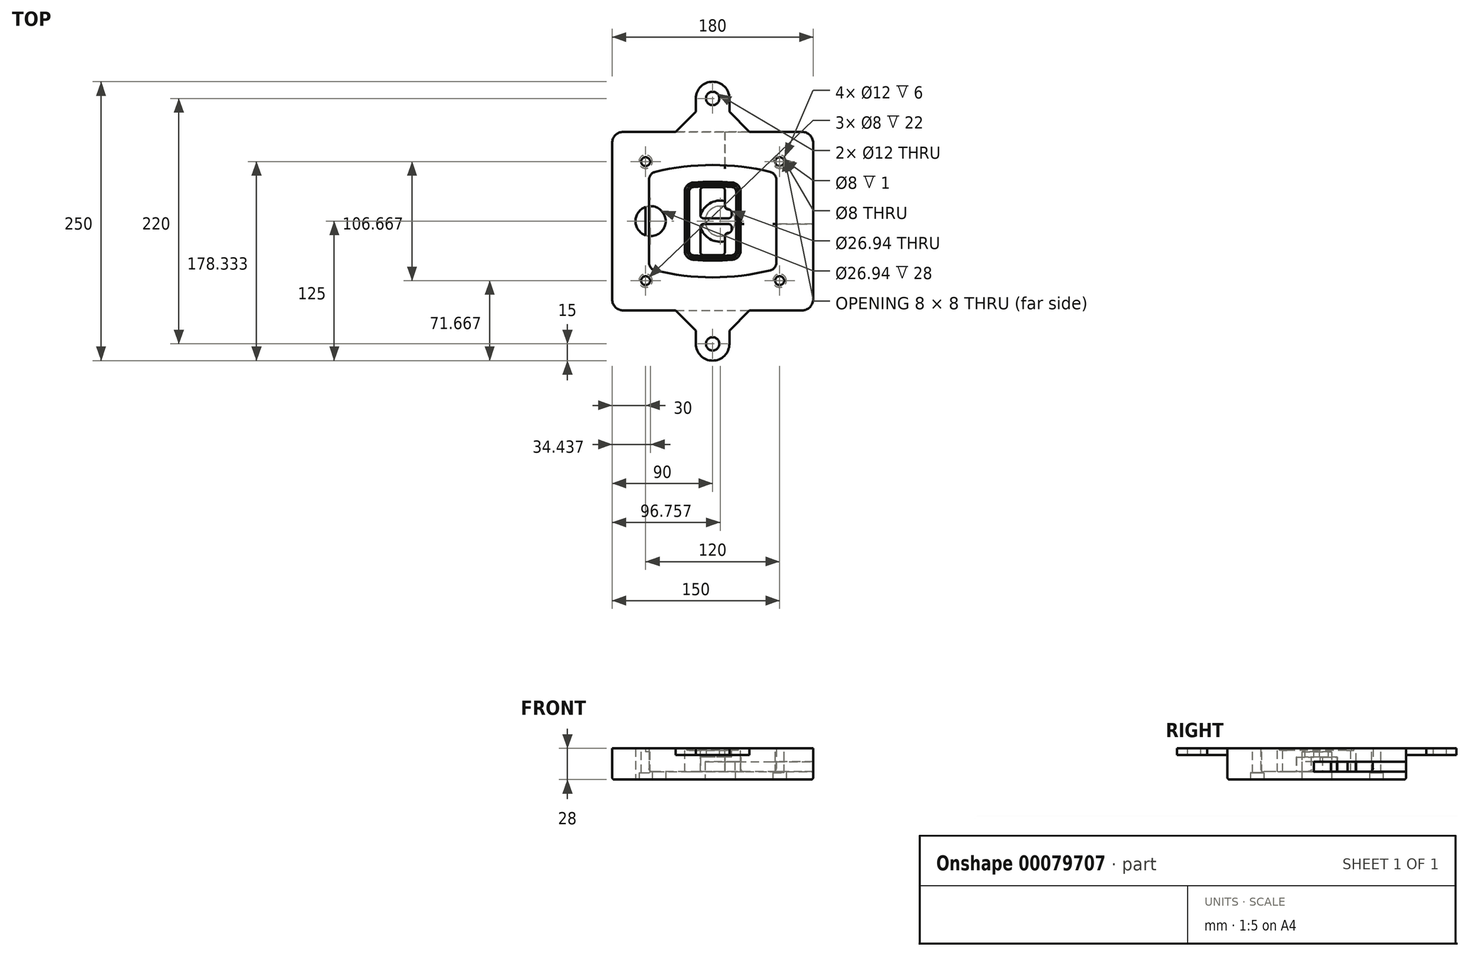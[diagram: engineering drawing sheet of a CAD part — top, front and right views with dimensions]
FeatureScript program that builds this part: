
annotation { "Feature Type Name" : "Feature", "Feature Type Description" : "" }
export const myFeature = defineFeature(function(context is Context, id is Id, definition is map)
    precondition{}
    {
        {
            var Q0;
            Q0=qCreatedBy(makeId("Top.planeOp"),FACE);
            var sketch = newSketch(context, id + "F0", { "sketchPlane" : qUnion([Q0])});
            skPoint(sketch, "E0.rect.middle", {"position": v(0, 0) * mm});
            skLineSegment(sketch, "E1.bottom", {"start": v(-80, -80) * mm, "end": v(80, -80) * mm});
            skLineSegment(sketch, "E1.top", {"start": v(-80, 80) * mm, "end": v(80, 80) * mm});
            skLineSegment(sketch, "E1.left", {"start": v(-90, -70) * mm, "end": v(-90, 70) * mm});
            skLineSegment(sketch, "E1.right", {"start": v(90, -70) * mm, "end": v(90, 70) * mm});
            skLineSegment(sketch, "E2", {"start": v(-90, 80) * mm, "end": v(90, -80) * mm, "construction": true});
            skLineSegment(sketch, "E3", {"start": v(90, 80) * mm, "end": v(-90, -80) * mm, "construction": true});
            skCircle(sketch, "E4", {"center": v(-60, 53.33) * mm, "radius": 4 * mm});
            skCircle(sketch, "E5", {"center": v(60, 53.33) * mm, "radius": 4 * mm});
            skCircle(sketch, "E6", {"center": v(60, -53.33) * mm, "radius": 4 * mm});
            skCircle(sketch, "E7", {"center": v(-60, -53.33) * mm, "radius": 4 * mm});
            skLineSegment(sketch, "E8", {"start": v(-60, 53.33) * mm, "end": v(60, 53.33) * mm, "construction": true});
            skLineSegment(sketch, "E9", {"start": v(60, 53.33) * mm, "end": v(60, -53.33) * mm, "construction": true});
            skLineSegment(sketch, "E10", {"start": v(60, -53.33) * mm, "end": v(-60, -53.33) * mm, "construction": true});
            skLineSegment(sketch, "E11", {"start": v(-60, -53.33) * mm, "end": v(-60, 53.33) * mm, "construction": true});
            skLineSegment(sketch, "E12", {"start": v(-60, 37.3) * mm, "end": v(-60, -37.3) * mm});
            skLineSegment(sketch, "E13", {"start": v(60, 37.3) * mm, "end": v(60, -37.3) * mm});
            skArc(sketch, "E14", {"start": v(52.38, 47.01) * mm, "mid": v(0, 53.33) * mm, "end": v(-52.38, 47.01) * mm});
            skArc(sketch, "E15", {"start": v(-52.38, -47.01) * mm, "mid": v(0, -53.33) * mm, "end": v(52.38, -47.01) * mm});
            skLineSegment(sketch, "E16", {"start": v(-60, 0) * mm, "end": v(60, 0) * mm, "construction": true});
            skPoint(sketch, "E17.visualSharp", {"position": v(-60, -45) * mm});
            skArc(sketch, "E17.filletArc", {"start": v(-60, -37.3) * mm, "mid": v(-57.87, -43.47) * mm, "end": v(-52.38, -47.01) * mm});
            skPoint(sketch, "E18.visualSharp", {"position": v(-60, 45) * mm});
            skArc(sketch, "E18.filletArc", {"start": v(-52.38, 47.01) * mm, "mid": v(-57.87, 43.47) * mm, "end": v(-60, 37.3) * mm});
            skPoint(sketch, "E19.visualSharp", {"position": v(60, 45) * mm});
            skArc(sketch, "E19.filletArc", {"start": v(60, 37.3) * mm, "mid": v(57.87, 43.47) * mm, "end": v(52.38, 47.01) * mm});
            skPoint(sketch, "E20.visualSharp", {"position": v(60, -45) * mm});
            skArc(sketch, "E20.filletArc", {"start": v(52.38, -47.01) * mm, "mid": v(57.87, -43.47) * mm, "end": v(60, -37.3) * mm});
            skPoint(sketch, "E21.visualSharp", {"position": v(-90, 80) * mm});
            skArc(sketch, "E21.filletArc", {"start": v(-80, 80) * mm, "mid": v(-87.07, 77.07) * mm, "end": v(-90, 70) * mm});
            skPoint(sketch, "E22.visualSharp", {"position": v(90, 80) * mm});
            skArc(sketch, "E22.filletArc", {"start": v(90, 70) * mm, "mid": v(87.07, 77.07) * mm, "end": v(80, 80) * mm});
            skPoint(sketch, "E23.visualSharp", {"position": v(90, -80) * mm});
            skArc(sketch, "E23.filletArc", {"start": v(80, -80) * mm, "mid": v(87.07, -77.07) * mm, "end": v(90, -70) * mm});
            skPoint(sketch, "E24.visualSharp", {"position": v(-90, -80) * mm});
            skArc(sketch, "E24.filletArc", {"start": v(-90, -70) * mm, "mid": v(-87.07, -77.07) * mm, "end": v(-80, -80) * mm});
            skArc(sketch, "E25.0", {"start": v(57, 37.3) * mm, "mid": v(55.5, 41.62) * mm, "end": v(51.67, 44.1) * mm});
            skLineSegment(sketch, "E25.1", {"start": v(57, 37.3) * mm, "end": v(57, -37.3) * mm});
            skArc(sketch, "E25.2", {"start": v(51.67, -44.1) * mm, "mid": v(55.5, -41.62) * mm, "end": v(57, -37.3) * mm});
            skArc(sketch, "E25.3", {"start": v(-51.67, -44.1) * mm, "mid": v(0, -50.33) * mm, "end": v(51.67, -44.1) * mm});
            skArc(sketch, "E25.4", {"start": v(-57, -37.3) * mm, "mid": v(-55.5, -41.62) * mm, "end": v(-51.67, -44.1) * mm});
            skArc(sketch, "E25.5", {"start": v(51.67, 44.1) * mm, "mid": v(0, 50.33) * mm, "end": v(-51.67, 44.1) * mm});
            skLineSegment(sketch, "E25.6", {"start": v(-57, 37.3) * mm, "end": v(-57, -37.3) * mm});
            skArc(sketch, "E25.7", {"start": v(-51.67, 44.1) * mm, "mid": v(-55.5, 41.62) * mm, "end": v(-57, 37.3) * mm});
            skArc(sketch, "E26.0", {"start": v(-53.33, 50.9) * mm, "mid": v(-61.01, 45.94) * mm, "end": v(-64, 37.3) * mm});
            skArc(sketch, "E26.1", {"start": v(53.33, 50.9) * mm, "mid": v(0, 57.33) * mm, "end": v(-53.33, 50.9) * mm});
            skArc(sketch, "E26.2", {"start": v(64, 37.3) * mm, "mid": v(61.01, 45.94) * mm, "end": v(53.33, 50.9) * mm});
            skLineSegment(sketch, "E26.3", {"start": v(64, 37.3) * mm, "end": v(64, -37.3) * mm});
            skArc(sketch, "E26.4", {"start": v(53.33, -50.9) * mm, "mid": v(61.01, -45.94) * mm, "end": v(64, -37.3) * mm});
            skLineSegment(sketch, "E26.5", {"start": v(-64, 37.3) * mm, "end": v(-64, -37.3) * mm});
            skArc(sketch, "E26.6", {"start": v(-53.33, -50.9) * mm, "mid": v(0, -57.33) * mm, "end": v(53.33, -50.9) * mm});
            skArc(sketch, "E26.7", {"start": v(-64, -37.3) * mm, "mid": v(-61.01, -45.94) * mm, "end": v(-53.33, -50.9) * mm});
            skSolve(sketch);
        }
        {
            var Q0;
            Q0=makeQuery(id+"F0.imprint","IMPRINT",FACE,{"disambiguationData":[TD([[makeQuery(id+"F0.imprint","IMPRINT",EDGE,{"derivedFrom":sQuery(id+"F0.wireOp",EDGE,"E1.bottom")}),1.0]])]});
            var Q1;
            Q1=makeQuery(id+"F0.imprint","IMPRINT",FACE,{"disambiguationData":[TD([[makeQuery(id+"F0.imprint","IMPRINT",EDGE,{"derivedFrom":sQuery(id+"F0.wireOp",EDGE,"E12")}),1.0]])]});
            var Q2;
            Q2=makeQuery(id+"F0.imprint","IMPRINT",FACE,{"disambiguationData":[TD([[makeQuery(id+"F0.imprint","IMPRINT",EDGE,{"derivedFrom":sQuery(id+"F0.wireOp",EDGE,"E25.0")}),1.0]])]});
            var Q3;
            Q3=makeQuery(id+"F0.imprint","IMPRINT",FACE,{"disambiguationData":[TD([[makeQuery(id+"F0.imprint","IMPRINT",EDGE,{"derivedFrom":sQuery(id+"F0.wireOp",EDGE,"E12")}),-1.0]])]});
            extrude(context, id + "F1", {"entities" : qUnion([Q0, Q1, Q2, Q3]), "oppositeDirection" : true, "depth" : 25 * mm});
        }
        {
            var Q0;
            Q0=makeQuery(id+"F0.imprint","IMPRINT",FACE,{"disambiguationData":[TD([[makeQuery(id+"F0.imprint","IMPRINT",EDGE,{"derivedFrom":sQuery(id+"F0.wireOp",EDGE,"E12")}),1.0]])]});
            extrude(context, id + "F2", {"entities" : qUnion([Q0]), "operationType" : NewBodyOperationType.ADD, "depth" : 3 * mm});
        }
        {
            var Q0;
            Q0=makeQuery(id+"F0.imprint","IMPRINT",FACE,{"disambiguationData":[TD([[makeQuery(id+"F0.imprint","IMPRINT",EDGE,{"derivedFrom":sQuery(id+"F0.wireOp",EDGE,"E25.0")}),1.0]])]});
            extrude(context, id + "F3", {"entities" : qUnion([Q0]), "operationType" : NewBodyOperationType.REMOVE, "oppositeDirection" : true, "depth" : 18 * mm});
        }
        {
            var Q0;
            Q0=makeQuery(id+"F2.opExtrude","CAP_FACE",FACE,{"disambiguationData":[OSD([sQuery(id+"F0.wireOp",EDGE,"E12"),sQuery(id+"F0.wireOp",EDGE,"E13"),sQuery(id+"F0.wireOp",EDGE,"E14"),sQuery(id+"F0.wireOp",EDGE,"E15"),sQuery(id+"F0.wireOp",EDGE,"E17.filletArc"),sQuery(id+"F0.wireOp",EDGE,"E18.filletArc"),sQuery(id+"F0.wireOp",EDGE,"E19.filletArc"),sQuery(id+"F0.wireOp",EDGE,"E20.filletArc"),sQuery(id+"F0.wireOp",EDGE,"E25.0"),sQuery(id+"F0.wireOp",EDGE,"E25.1"),sQuery(id+"F0.wireOp",EDGE,"E25.2"),sQuery(id+"F0.wireOp",EDGE,"E25.3"),sQuery(id+"F0.wireOp",EDGE,"E25.4"),sQuery(id+"F0.wireOp",EDGE,"E25.5"),sQuery(id+"F0.wireOp",EDGE,"E25.6"),sQuery(id+"F0.wireOp",EDGE,"E25.7")])],"isStart":false});
            var sketch = newSketch(context, id + "F4", { "sketchPlane" : qUnion([Q0])});
            skArc(sketch, "E27.0", {"start": v(-17.7, -34.56) * mm, "mid": v(0, -35.33) * mm, "end": v(17.7, -34.56) * mm});
            skArc(sketch, "E28.0", {"start": v(17.7, 34.56) * mm, "mid": v(0, 35.33) * mm, "end": v(-17.7, 34.56) * mm});
            skLineSegment(sketch, "E29", {"start": v(-25, 26.59) * mm, "end": v(-25, -26.59) * mm});
            skLineSegment(sketch, "E30", {"start": v(25, 26.59) * mm, "end": v(25, -26.59) * mm});
            skLineSegment(sketch, "E31", {"start": v(-25, 33.78) * mm, "end": v(25, 33.78) * mm, "construction": true});
            skLineSegment(sketch, "E32", {"start": v(-25, -33.78) * mm, "end": v(25, -33.78) * mm, "construction": true});
            skPoint(sketch, "E33.visualSharp", {"position": v(-25, 33.78) * mm});
            skArc(sketch, "E33.filletArc", {"start": v(-17.7, 34.56) * mm, "mid": v(-22.9, 32) * mm, "end": v(-25, 26.59) * mm});
            skPoint(sketch, "E34.visualSharp", {"position": v(25, 33.78) * mm});
            skArc(sketch, "E34.filletArc", {"start": v(25, 26.59) * mm, "mid": v(22.9, 32) * mm, "end": v(17.7, 34.56) * mm});
            skPoint(sketch, "E35.visualSharp", {"position": v(25, -33.78) * mm});
            skArc(sketch, "E35.filletArc", {"start": v(17.7, -34.56) * mm, "mid": v(22.9, -32) * mm, "end": v(25, -26.59) * mm});
            skPoint(sketch, "E36.visualSharp", {"position": v(-25, -33.78) * mm});
            skArc(sketch, "E36.filletArc", {"start": v(-25, -26.59) * mm, "mid": v(-22.9, -32) * mm, "end": v(-17.7, -34.56) * mm});
            skArc(sketch, "E37.0", {"start": v(51.67, 44.1) * mm, "mid": v(0, 50.33) * mm, "end": v(-51.67, 44.1) * mm});
            skArc(sketch, "E37.1", {"start": v(-51.67, 44.1) * mm, "mid": v(-55.5, 41.62) * mm, "end": v(-57, 37.3) * mm});
            skLineSegment(sketch, "E37.2", {"start": v(-57, 37.3) * mm, "end": v(-57, -37.3) * mm});
            skArc(sketch, "E37.3", {"start": v(-57, -37.3) * mm, "mid": v(-55.5, -41.62) * mm, "end": v(-51.67, -44.1) * mm});
            skArc(sketch, "E37.4", {"start": v(-51.67, -44.1) * mm, "mid": v(0, -50.33) * mm, "end": v(51.67, -44.1) * mm});
            skArc(sketch, "E37.5", {"start": v(51.67, -44.1) * mm, "mid": v(55.5, -41.62) * mm, "end": v(57, -37.3) * mm});
            skLineSegment(sketch, "E37.6", {"start": v(57, 37.3) * mm, "end": v(57, -37.3) * mm});
            skArc(sketch, "E37.7", {"start": v(57, 37.3) * mm, "mid": v(55.5, 41.62) * mm, "end": v(51.67, 44.1) * mm});
            skLineSegment(sketch, "E38.0", {"start": v(23, 26.59) * mm, "end": v(23, -26.59) * mm});
            skArc(sketch, "E38.1", {"start": v(17.53, -32.56) * mm, "mid": v(21.42, -30.64) * mm, "end": v(23, -26.59) * mm});
            skArc(sketch, "E38.2", {"start": v(-17.53, -32.56) * mm, "mid": v(0, -33.33) * mm, "end": v(17.53, -32.56) * mm});
            skArc(sketch, "E38.3", {"start": v(-23, -26.59) * mm, "mid": v(-21.42, -30.64) * mm, "end": v(-17.53, -32.56) * mm});
            skLineSegment(sketch, "E38.4", {"start": v(-23, 26.59) * mm, "end": v(-23, -26.59) * mm});
            skArc(sketch, "E38.5", {"start": v(23, 26.59) * mm, "mid": v(21.42, 30.64) * mm, "end": v(17.53, 32.56) * mm});
            skArc(sketch, "E38.6", {"start": v(-17.53, 32.56) * mm, "mid": v(-21.42, 30.64) * mm, "end": v(-23, 26.59) * mm});
            skArc(sketch, "E38.7", {"start": v(17.53, 32.56) * mm, "mid": v(0, 33.33) * mm, "end": v(-17.53, 32.56) * mm});
            skArc(sketch, "E39.0", {"start": v(21, 26.59) * mm, "mid": v(19.95, 29.29) * mm, "end": v(17.35, 30.57) * mm});
            skLineSegment(sketch, "E39.1", {"start": v(21, 26.59) * mm, "end": v(21, -26.59) * mm});
            skArc(sketch, "E39.2", {"start": v(17.35, -30.57) * mm, "mid": v(19.95, -29.29) * mm, "end": v(21, -26.59) * mm});
            skArc(sketch, "E39.3", {"start": v(-17.35, -30.57) * mm, "mid": v(0, -31.33) * mm, "end": v(17.35, -30.57) * mm});
            skArc(sketch, "E39.4", {"start": v(-21, -26.59) * mm, "mid": v(-19.95, -29.29) * mm, "end": v(-17.35, -30.57) * mm});
            skArc(sketch, "E39.5", {"start": v(17.35, 30.57) * mm, "mid": v(0, 31.33) * mm, "end": v(-17.35, 30.57) * mm});
            skLineSegment(sketch, "E39.6", {"start": v(-21, 26.59) * mm, "end": v(-21, -26.59) * mm});
            skArc(sketch, "E39.7", {"start": v(-17.35, 30.57) * mm, "mid": v(-19.95, 29.29) * mm, "end": v(-21, 26.59) * mm});
            skLineSegment(sketch, "E40", {"start": v(-25, 0) * mm, "end": v(25, 0) * mm, "construction": true});
            skLineSegment(sketch, "E41", {"start": v(-11, 5.5) * mm, "end": v(-11, 27.5) * mm});
            skLineSegment(sketch, "E42", {"start": v(-8, 30.5) * mm, "end": v(8, 30.5) * mm});
            skLineSegment(sketch, "E43", {"start": v(11, 27.5) * mm, "end": v(11, 13.5) * mm});
            skLineSegment(sketch, "E44", {"start": v(14, 10.5) * mm, "end": v(14, 10.5) * mm});
            skLineSegment(sketch, "E45", {"start": v(17, 7.5) * mm, "end": v(17, 5.5) * mm});
            skLineSegment(sketch, "E46", {"start": v(14, 2.5) * mm, "end": v(-8, 2.5) * mm});
            skPoint(sketch, "E47.visualSharp", {"position": v(-11, 30.5) * mm});
            skArc(sketch, "E47.filletArc", {"start": v(-8, 30.5) * mm, "mid": v(-10.12, 29.62) * mm, "end": v(-11, 27.5) * mm});
            skPoint(sketch, "E48.visualSharp", {"position": v(11, 30.5) * mm});
            skArc(sketch, "E48.filletArc", {"start": v(11, 27.5) * mm, "mid": v(10.12, 29.62) * mm, "end": v(8, 30.5) * mm});
            skPoint(sketch, "E49.visualSharp", {"position": v(11, 10.5) * mm});
            skArc(sketch, "E49.filletArc", {"start": v(11, 13.5) * mm, "mid": v(11.88, 11.38) * mm, "end": v(14, 10.5) * mm});
            skPoint(sketch, "E50.visualSharp", {"position": v(17, 10.5) * mm});
            skArc(sketch, "E50.filletArc", {"start": v(17, 7.5) * mm, "mid": v(16.12, 9.62) * mm, "end": v(14, 10.5) * mm});
            skPoint(sketch, "E51.visualSharp", {"position": v(17, 2.5) * mm});
            skArc(sketch, "E51.filletArc", {"start": v(14, 2.5) * mm, "mid": v(16.12, 3.38) * mm, "end": v(17, 5.5) * mm});
            skPoint(sketch, "E52.visualSharp", {"position": v(-11, 2.5) * mm});
            skArc(sketch, "E52.filletArc", {"start": v(-11, 5.5) * mm, "mid": v(-10.12, 3.38) * mm, "end": v(-8, 2.5) * mm});
            skLineSegment(sketch, "E53.0.MirrorCS", {"start": v(14, -2.5) * mm, "end": v(-8, -2.5) * mm});
            skArc(sketch, "E54.0.MirrorCS", {"start": v(-11, -5.5) * mm, "mid": v(-10.12, -3.38) * mm, "end": v(-8, -2.5) * mm});
            skLineSegment(sketch, "E55.0.MirrorCS", {"start": v(-11, -5.5) * mm, "end": v(-11, -27.5) * mm});
            skArc(sketch, "E56.0.MirrorCS", {"start": v(-8, -30.5) * mm, "mid": v(-10.12, -29.62) * mm, "end": v(-11, -27.5) * mm});
            skLineSegment(sketch, "E57.0.MirrorCS", {"start": v(-8, -30.5) * mm, "end": v(8, -30.5) * mm});
            skArc(sketch, "E58.0.MirrorCS", {"start": v(11, -27.5) * mm, "mid": v(10.12, -29.62) * mm, "end": v(8, -30.5) * mm});
            skLineSegment(sketch, "E59.0.MirrorCS", {"start": v(11, -27.5) * mm, "end": v(11, -13.5) * mm});
            skArc(sketch, "E60.0.MirrorCS", {"start": v(11, -13.5) * mm, "mid": v(11.88, -11.38) * mm, "end": v(14, -10.5) * mm});
            skArc(sketch, "E61.0.MirrorCS", {"start": v(17, -7.5) * mm, "mid": v(16.12, -9.62) * mm, "end": v(14, -10.5) * mm});
            skLineSegment(sketch, "E62.0.MirrorCS", {"start": v(17, -7.5) * mm, "end": v(17, -5.5) * mm});
            skArc(sketch, "E63.0.MirrorCS", {"start": v(14, -2.5) * mm, "mid": v(16.12, -3.38) * mm, "end": v(17, -5.5) * mm});
            skSolve(sketch);
        }
        {
            var Q0;
            Q0=makeQuery(id+"F4.imprint","IMPRINT",FACE,{"disambiguationData":[TD([[makeQuery(id+"F4.imprint","IMPRINT",EDGE,{"derivedFrom":sQuery(id+"F4.wireOp",EDGE,"E27.0")}),1.0]])]});
            var Q1;
            Q1=makeQuery(id+"F4.imprint","IMPRINT",FACE,{"disambiguationData":[TD([[makeQuery(id+"F4.imprint","IMPRINT",EDGE,{"derivedFrom":sQuery(id+"F4.wireOp",EDGE,"E38.0")}),-1.0]])]});
            var Q2;
            Q2=makeQuery(id+"F4.imprint","IMPRINT",FACE,{"disambiguationData":[TD([[makeQuery(id+"F4.imprint","IMPRINT",EDGE,{"derivedFrom":sQuery(id+"F4.wireOp",EDGE,"E39.0")}),1.0]])]});
            extrude(context, id + "F5", {"entities" : qUnion([Q0, Q1, Q2]), "operationType" : NewBodyOperationType.ADD, "endBound" : BoundingType.UP_TO_NEXT, "oppositeDirection" : true, "depth" : 25 * mm});
        }
        {
            var Q0;
            Q0=makeQuery(id+"F4.imprint","IMPRINT",FACE,{"disambiguationData":[TD([[makeQuery(id+"F4.imprint","IMPRINT",EDGE,{"derivedFrom":sQuery(id+"F4.wireOp",EDGE,"E38.0")}),-1.0]])]});
            extrude(context, id + "F6", {"entities" : qUnion([Q0]), "operationType" : NewBodyOperationType.REMOVE, "oppositeDirection" : true, "depth" : 2 * mm});
        }
        {
            var Q0;
            Q0=makeQuery(id+"F1.opExtrude","CAP_FACE",FACE,{"disambiguationData":[OSD([sQuery(id+"F0.wireOp",EDGE,"E1.bottom"),sQuery(id+"F0.wireOp",EDGE,"E1.top"),sQuery(id+"F0.wireOp",EDGE,"E1.left"),sQuery(id+"F0.wireOp",EDGE,"E1.right"),sQuery(id+"F0.wireOp",EDGE,"E4"),sQuery(id+"F0.wireOp",EDGE,"E5"),sQuery(id+"F0.wireOp",EDGE,"E6"),sQuery(id+"F0.wireOp",EDGE,"E7"),sQuery(id+"F0.wireOp",EDGE,"E21.filletArc"),sQuery(id+"F0.wireOp",EDGE,"E22.filletArc"),sQuery(id+"F0.wireOp",EDGE,"E23.filletArc"),sQuery(id+"F0.wireOp",EDGE,"E24.filletArc")])],"isStart":false});
            var sketch = newSketch(context, id + "F7", { "sketchPlane" : qUnion([Q0])});
            skCircle(sketch, "E64", {"center": v(6.76, 0) * mm, "radius": 13.47 * mm});
            skCircle(sketch, "E65", {"center": v(-55.56, 0) * mm, "radius": 13.47 * mm});
            skLineSegment(sketch, "E66", {"start": v(90, 0) * mm, "end": v(-90, 0) * mm});
            skCircle(sketch, "E67", {"center": v(6.76, 0) * mm, "radius": 18.47 * mm});
            skCircle(sketch, "E68", {"center": v(60, -53.33) * mm, "radius": 6 * mm});
            skCircle(sketch, "E69", {"center": v(-60, -53.33) * mm, "radius": 6 * mm});
            skCircle(sketch, "E70", {"center": v(-60, 53.33) * mm, "radius": 6 * mm});
            skCircle(sketch, "E71", {"center": v(60, 53.33) * mm, "radius": 6 * mm});
            skSolve(sketch);
        }
        {
            var Q0;
            {var subQ1=sQuery(id+"F7.wireOp",EDGE,"E66");var subQ4=sQuery(id+"F7.wireOp",EDGE,"E64");var subQ6=makeQuery(id+"F7.imprint","INTERSECT",VERTEX,{"disambiguationData":[OD(0.0)],"derivedFrom":[subQ4,subQ1]});Q0=makeQuery(id+"F7.imprint","IMPRINT",FACE,{"disambiguationData":[TD([[makeQuery(id+"F7.imprint","IMPRINT",EDGE,{"disambiguationData":[TD([[subQ6,-1.0]])],"derivedFrom":subQ4}),-1.0]])]});}
            var Q1;
            {var subQ0=sQuery(id+"F7.wireOp",EDGE,"E66");var subQ1=sQuery(id+"F7.wireOp",EDGE,"E64");var subQ3=makeQuery(id+"F7.imprint","INTERSECT",VERTEX,{"disambiguationData":[OD(0.0)],"derivedFrom":[subQ1,subQ0]});Q1=makeQuery(id+"F7.imprint","IMPRINT",FACE,{"disambiguationData":[TD([[makeQuery(id+"F7.imprint","IMPRINT",EDGE,{"disambiguationData":[TD([[subQ3,-1.0]])],"derivedFrom":subQ1}),1.0]])]});}
            var Q2;
            {var subQ0=sQuery(id+"F7.wireOp",EDGE,"E66");var subQ1=sQuery(id+"F7.wireOp",EDGE,"E64");var subQ3=makeQuery(id+"F7.imprint","INTERSECT",VERTEX,{"disambiguationData":[OD(0.0)],"derivedFrom":[subQ1,subQ0]});Q2=makeQuery(id+"F7.imprint","IMPRINT",FACE,{"disambiguationData":[TD([[makeQuery(id+"F7.imprint","IMPRINT",EDGE,{"disambiguationData":[TD([[subQ3,1.0]])],"derivedFrom":subQ1}),1.0]])]});}
            var Q3;
            {var subQ1=sQuery(id+"F7.wireOp",EDGE,"E66");var subQ4=sQuery(id+"F7.wireOp",EDGE,"E64");var subQ6=makeQuery(id+"F7.imprint","INTERSECT",VERTEX,{"disambiguationData":[OD(0.0)],"derivedFrom":[subQ4,subQ1]});Q3=makeQuery(id+"F7.imprint","IMPRINT",FACE,{"disambiguationData":[TD([[makeQuery(id+"F7.imprint","IMPRINT",EDGE,{"disambiguationData":[TD([[subQ6,1.0]])],"derivedFrom":subQ4}),-1.0]])]});}
            extrude(context, id + "F8", {"entities" : qUnion([Q0, Q1, Q2, Q3]), "operationType" : NewBodyOperationType.ADD, "oppositeDirection" : true, "depth" : 20 * mm});
        }
        {
            var Q0;
            {var subQ0=sQuery(id+"F7.wireOp",EDGE,"E66");var subQ1=sQuery(id+"F7.wireOp",EDGE,"E64");var subQ3=makeQuery(id+"F7.imprint","INTERSECT",VERTEX,{"disambiguationData":[OD(0.0)],"derivedFrom":[subQ1,subQ0]});Q0=makeQuery(id+"F7.imprint","IMPRINT",FACE,{"disambiguationData":[TD([[makeQuery(id+"F7.imprint","IMPRINT",EDGE,{"disambiguationData":[TD([[subQ3,-1.0]])],"derivedFrom":subQ1}),1.0]])]});}
            var Q1;
            {var subQ0=sQuery(id+"F7.wireOp",EDGE,"E66");var subQ1=sQuery(id+"F7.wireOp",EDGE,"E64");var subQ3=makeQuery(id+"F7.imprint","INTERSECT",VERTEX,{"disambiguationData":[OD(0.0)],"derivedFrom":[subQ1,subQ0]});Q1=makeQuery(id+"F7.imprint","IMPRINT",FACE,{"disambiguationData":[TD([[makeQuery(id+"F7.imprint","IMPRINT",EDGE,{"disambiguationData":[TD([[subQ3,1.0]])],"derivedFrom":subQ1}),1.0]])]});}
            extrude(context, id + "F9", {"entities" : qUnion([Q0, Q1]), "operationType" : NewBodyOperationType.REMOVE, "oppositeDirection" : true, "depth" : 16 * mm});
        }
        {
            var Q0;
            {var subQ0=sQuery(id+"F7.wireOp",EDGE,"E66");var subQ1=sQuery(id+"F7.wireOp",EDGE,"E65");var subQ3=makeQuery(id+"F7.imprint","INTERSECT",VERTEX,{"disambiguationData":[OD(0.0)],"derivedFrom":[subQ1,subQ0]});Q0=makeQuery(id+"F7.imprint","IMPRINT",FACE,{"disambiguationData":[TD([[makeQuery(id+"F7.imprint","IMPRINT",EDGE,{"disambiguationData":[TD([[subQ3,-1.0]])],"derivedFrom":subQ1}),1.0]])]});}
            var Q1;
            {var subQ0=sQuery(id+"F7.wireOp",EDGE,"E66");var subQ1=sQuery(id+"F7.wireOp",EDGE,"E65");var subQ3=makeQuery(id+"F7.imprint","INTERSECT",VERTEX,{"disambiguationData":[OD(0.0)],"derivedFrom":[subQ1,subQ0]});Q1=makeQuery(id+"F7.imprint","IMPRINT",FACE,{"disambiguationData":[TD([[makeQuery(id+"F7.imprint","IMPRINT",EDGE,{"disambiguationData":[TD([[subQ3,1.0]])],"derivedFrom":subQ1}),1.0]])]});}
            extrude(context, id + "F10", {"entities" : qUnion([Q0, Q1]), "operationType" : NewBodyOperationType.REMOVE, "oppositeDirection" : true, "depth" : 25 * mm});
        }
        {
            var Q0;
            Q0=makeQuery(id+"F7.imprint","IMPRINT",FACE,{"disambiguationData":[TD([[makeQuery(id+"F7.imprint","IMPRINT",EDGE,{"derivedFrom":sQuery(id+"F7.wireOp",EDGE,"E68")}),1.0]])]});
            var Q1;
            Q1=makeQuery(id+"F7.imprint","IMPRINT",FACE,{"disambiguationData":[TD([[makeQuery(id+"F7.imprint","IMPRINT",EDGE,{"derivedFrom":makeQuery(id+"F1.opExtrude","CAP_EDGE",EDGE,{"disambiguationData":[OSD([sQuery(id+"F0.wireOp",EDGE,"E5")])],"isStart":false})}),-1.0]])]});
            var Q2;
            Q2=makeQuery(id+"F7.imprint","IMPRINT",FACE,{"disambiguationData":[TD([[makeQuery(id+"F7.imprint","IMPRINT",EDGE,{"derivedFrom":sQuery(id+"F7.wireOp",EDGE,"E69")}),1.0]])]});
            var Q3;
            Q3=makeQuery(id+"F7.imprint","IMPRINT",FACE,{"disambiguationData":[TD([[makeQuery(id+"F7.imprint","IMPRINT",EDGE,{"derivedFrom":makeQuery(id+"F1.opExtrude","CAP_EDGE",EDGE,{"disambiguationData":[OSD([sQuery(id+"F0.wireOp",EDGE,"E4")])],"isStart":false})}),-1.0]])]});
            var Q4;
            Q4=makeQuery(id+"F7.imprint","IMPRINT",FACE,{"disambiguationData":[TD([[makeQuery(id+"F7.imprint","IMPRINT",EDGE,{"derivedFrom":sQuery(id+"F7.wireOp",EDGE,"E70")}),1.0]])]});
            var Q5;
            Q5=makeQuery(id+"F7.imprint","IMPRINT",FACE,{"disambiguationData":[TD([[makeQuery(id+"F7.imprint","IMPRINT",EDGE,{"derivedFrom":makeQuery(id+"F1.opExtrude","CAP_EDGE",EDGE,{"disambiguationData":[OSD([sQuery(id+"F0.wireOp",EDGE,"E7")])],"isStart":false})}),-1.0]])]});
            var Q6;
            Q6=makeQuery(id+"F7.imprint","IMPRINT",FACE,{"disambiguationData":[TD([[makeQuery(id+"F7.imprint","IMPRINT",EDGE,{"derivedFrom":sQuery(id+"F7.wireOp",EDGE,"E71")}),1.0]])]});
            var Q7;
            Q7=makeQuery(id+"F7.imprint","IMPRINT",FACE,{"disambiguationData":[TD([[makeQuery(id+"F7.imprint","IMPRINT",EDGE,{"derivedFrom":makeQuery(id+"F1.opExtrude","CAP_EDGE",EDGE,{"disambiguationData":[OSD([sQuery(id+"F0.wireOp",EDGE,"E6")])],"isStart":false})}),-1.0]])]});
            extrude(context, id + "F11", {"entities" : qUnion([Q0, Q1, Q2, Q3, Q4, Q5, Q6, Q7]), "operationType" : NewBodyOperationType.REMOVE, "oppositeDirection" : true, "depth" : 6 * mm});
        }
        {
            var Q0;
            Q0=makeQuery(id+"F9.boolean.opBoolean","COPY",FACE,{"derivedFrom":makeQuery(id+"F9.opExtrude","CAP_FACE",FACE,{"disambiguationData":[OSD([sQuery(id+"F7.wireOp",EDGE,"E64")])],"isStart":false})});
            var sketch = newSketch(context, id + "F12", { "sketchPlane" : qUnion([Q0])});
            skArc(sketch, "E72.0", {"start": v(11, -88.19) * mm, "mid": v(97.1, -83.6) * mm, "end": v(92.5, 2.5) * mm});
            skLineSegment(sketch, "E72.1", {"start": v(11, -17.97) * mm, "end": v(11, -17.97) * mm});
            skLineSegment(sketch, "E73", {"start": v(92.5, -105.13) * mm, "end": v(102.3, -105.13) * mm});
            skLineSegment(sketch, "E74.0", {"start": v(92.5, 2.5) * mm, "end": v(14, 2.5) * mm});
            skArc(sketch, "E74.1", {"start": v(14, 2.5) * mm, "mid": v(16.12, 3.38) * mm, "end": v(17, 5.5) * mm});
            skLineSegment(sketch, "E74.2", {"start": v(17, 7.5) * mm, "end": v(17, 5.5) * mm});
            skArc(sketch, "E74.3", {"start": v(17, 7.5) * mm, "mid": v(16.12, 9.62) * mm, "end": v(14, 10.5) * mm});
            skArc(sketch, "E74.4", {"start": v(11, 13.5) * mm, "mid": v(11.88, 11.38) * mm, "end": v(14, 10.5) * mm});
            skLineSegment(sketch, "E74.5", {"start": v(11, 13.5) * mm, "end": v(11, -88.19) * mm});
            skLineSegment(sketch, "E74.7", {"start": v(92.5, -2.5) * mm, "end": v(14, -2.5) * mm});
            skArc(sketch, "E74.8", {"start": v(14, -2.5) * mm, "mid": v(16.12, -3.38) * mm, "end": v(17, -5.5) * mm});
            skLineSegment(sketch, "E74.9", {"start": v(17, -7.5) * mm, "end": v(17, -5.5) * mm});
            skArc(sketch, "E74.10", {"start": v(17, -7.5) * mm, "mid": v(16.12, -9.62) * mm, "end": v(14, -10.5) * mm});
            skArc(sketch, "E74.11", {"start": v(11, -13.5) * mm, "mid": v(11.88, -11.38) * mm, "end": v(14, -10.5) * mm});
            skLineSegment(sketch, "E74.12", {"start": v(11, -17.97) * mm, "end": v(11, -13.5) * mm});
            skPoint(sketch, "E75.orphan", {"position": v(11, -27.5) * mm});
            skPoint(sketch, "E76.orphan", {"position": v(-8, -2.5) * mm});
            skPoint(sketch, "E77.orphan", {"position": v(-8, 2.5) * mm});
            skPoint(sketch, "E78.orphan", {"position": v(11, 27.5) * mm});
            skSolve(sketch);
        }
        {
            var Q0;
            {var subQ7=sQuery(id+"F12.wireOp",EDGE,"E72.0");var subQ14=sQuery(id+"F12.wireOp",EDGE,"E72.1");var subQ16=sQuery(id+"F12.wireOp",EDGE,"E74.1");var subQ18=sQuery(id+"F12.wireOp",EDGE,"E74.8");Q0=qUnion([makeQuery(id+"F12.imprint","IMPRINT",FACE,{"disambiguationData":[TD([[makeQuery(id+"F12.imprint","IMPRINT",EDGE,{"derivedFrom":subQ7}),1.0]])]}),makeQuery(id+"F12.imprint","IMPRINT",FACE,{"disambiguationData":[TD([[makeQuery(id+"F12.imprint","IMPRINT",EDGE,{"derivedFrom":subQ14}),1.0]])]}),makeQuery(id+"F12.imprint","IMPRINT",FACE,{"disambiguationData":[TD([[makeQuery(id+"F12.imprint","IMPRINT",EDGE,{"derivedFrom":subQ16}),1.0]])]}),makeQuery(id+"F12.imprint","IMPRINT",FACE,{"disambiguationData":[TD([[makeQuery(id+"F12.imprint","IMPRINT",EDGE,{"derivedFrom":subQ18}),-1.0]])]})]);}
            var Q1;
            Q1=makeQuery(id+"F5.boolean.opBoolean","SPLIT",FACE,{"disambiguationData":[TD([makeQuery(id+"F5.opExtrude","SWEPT_FACE",FACE,{"disambiguationData":[OSD([sQuery(id+"F4.wireOp",EDGE,"E41")])]})])],"derivedFrom":makeQuery(id+"F3.boolean.opBoolean","COPY",FACE,{"derivedFrom":makeQuery(id+"F3.opExtrude","CAP_FACE",FACE,{"disambiguationData":[OSD([sQuery(id+"F0.wireOp",EDGE,"E25.0"),sQuery(id+"F0.wireOp",EDGE,"E25.1"),sQuery(id+"F0.wireOp",EDGE,"E25.2"),sQuery(id+"F0.wireOp",EDGE,"E25.3"),sQuery(id+"F0.wireOp",EDGE,"E25.4"),sQuery(id+"F0.wireOp",EDGE,"E25.5"),sQuery(id+"F0.wireOp",EDGE,"E25.6"),sQuery(id+"F0.wireOp",EDGE,"E25.7")])],"isStart":false})})});
            extrude(context, id + "F13", {"entities" : qUnion([Q0]), "operationType" : NewBodyOperationType.REMOVE, "endBound" : BoundingType.UP_TO_SURFACE, "endBoundEntityFace" : qUnion([Q1]), "depth" : 25 * mm});
        }
        {
            var Q0;
            Q0=makeQuery(id+"F3.boolean.opBoolean","COPY",EDGE,{"derivedFrom":makeQuery(id+"F3.opExtrude","CAP_EDGE",EDGE,{"disambiguationData":[OSD([sQuery(id+"F0.wireOp",EDGE,"E25.6")])],"isStart":false})});
            var Q1;
            Q1=makeQuery(id+"F8.boolean.opBoolean","INTERSECT",EDGE,{"derivedFrom":[makeQuery(id+"F5.opExtrude","SWEPT_FACE",FACE,{"disambiguationData":[OSD([sQuery(id+"F4.wireOp",EDGE,"E30")])]}),makeQuery(id+"F8.opExtrude","CAP_FACE",FACE,{"disambiguationData":[OSD([sQuery(id+"F7.wireOp",EDGE,"E67")])],"isStart":false})]});
            var Q2;
            Q2=makeQuery(id+"F8.boolean.opBoolean","INTERSECT",EDGE,{"disambiguationData":[OD(1.0)],"derivedFrom":[makeQuery(id+"F5.opExtrude","SWEPT_FACE",FACE,{"disambiguationData":[OSD([sQuery(id+"F4.wireOp",EDGE,"E30")])]}),makeQuery(id+"F8.opExtrude","SWEPT_FACE",FACE,{"disambiguationData":[OSD([sQuery(id+"F7.wireOp",EDGE,"E67")])]})]});
            var Q3;
            {var subQ0=makeQuery(id+"F3.boolean.opBoolean","COPY",FACE,{"derivedFrom":makeQuery(id+"F3.opExtrude","CAP_FACE",FACE,{"disambiguationData":[OSD([sQuery(id+"F0.wireOp",EDGE,"E25.0"),sQuery(id+"F0.wireOp",EDGE,"E25.1"),sQuery(id+"F0.wireOp",EDGE,"E25.2"),sQuery(id+"F0.wireOp",EDGE,"E25.3"),sQuery(id+"F0.wireOp",EDGE,"E25.4"),sQuery(id+"F0.wireOp",EDGE,"E25.5"),sQuery(id+"F0.wireOp",EDGE,"E25.6"),sQuery(id+"F0.wireOp",EDGE,"E25.7")])],"isStart":false})});var subQ1=sQuery(id+"F4.wireOp",EDGE,"E30");Q3=makeQuery(id+"F8.boolean.opBoolean","SPLIT",EDGE,{"disambiguationData":[TD([makeQuery(id+"F5.opExtrude","SWEPT_FACE",FACE,{"disambiguationData":[OSD([sQuery(id+"F4.wireOp",EDGE,"E35.filletArc")])]})])],"derivedFrom":makeQuery(id+"F5.opExtrude","TWEAK_EDGE",EDGE,{"derivedFrom":[subQ0,makeQuery(id+"F4.imprint","IMPRINT",EDGE,{"derivedFrom":subQ1})]})});}
            var Q4;
            {var subQ0=sQuery(id+"F0.wireOp",EDGE,"E25.0");var subQ1=sQuery(id+"F0.wireOp",EDGE,"E25.1");var subQ2=sQuery(id+"F0.wireOp",EDGE,"E25.2");var subQ3=sQuery(id+"F0.wireOp",EDGE,"E25.3");var subQ4=sQuery(id+"F0.wireOp",EDGE,"E25.4");var subQ5=sQuery(id+"F0.wireOp",EDGE,"E25.5");var subQ6=sQuery(id+"F0.wireOp",EDGE,"E25.6");var subQ7=sQuery(id+"F0.wireOp",EDGE,"E25.7");Q4=makeQuery(id+"F8.boolean.opBoolean","INTERSECT",EDGE,{"derivedFrom":[makeQuery(id+"F5.boolean.opBoolean","SPLIT",FACE,{"disambiguationData":[TD([makeQuery(id+"F2.opExtrude","SWEPT_FACE",FACE,{"disambiguationData":[OSD([subQ0])]})])],"derivedFrom":makeQuery(id+"F3.boolean.opBoolean","COPY",FACE,{"derivedFrom":makeQuery(id+"F3.opExtrude","CAP_FACE",FACE,{"disambiguationData":[OSD([subQ0,subQ1,subQ2,subQ3,subQ4,subQ5,subQ6,subQ7])],"isStart":false})})}),makeQuery(id+"F8.opExtrude","SWEPT_FACE",FACE,{"disambiguationData":[OSD([sQuery(id+"F7.wireOp",EDGE,"E67")])]})]});}
            var Q5;
            Q5=makeQuery(id+"F8.boolean.opBoolean","INTERSECT",EDGE,{"disambiguationData":[OD(0.0)],"derivedFrom":[makeQuery(id+"F5.opExtrude","SWEPT_FACE",FACE,{"disambiguationData":[OSD([sQuery(id+"F4.wireOp",EDGE,"E30")])]}),makeQuery(id+"F8.opExtrude","SWEPT_FACE",FACE,{"disambiguationData":[OSD([sQuery(id+"F7.wireOp",EDGE,"E67")])]})]});
            fillet(context, id + "F14", {"entities" : qUnion([Q0, Q1, Q2, Q3, Q4, Q5]), "radius" : 3 * mm, "tangentPropagation" : true, "allowEdgeOverflow" : false});
        }
        {
            var Q0;
            Q0=makeQuery(id+"F1.opExtrude","CAP_EDGE",EDGE,{"disambiguationData":[OSD([sQuery(id+"F0.wireOp",EDGE,"E1.bottom")])],"isStart":false});
            fillet(context, id + "F15", {"entities" : qUnion([Q0]), "radius" : 2 * mm, "tangentPropagation" : true, "allowEdgeOverflow" : false});
        }
        {
            var Q0;
            {var subQ0=sQuery(id+"F0.wireOp",EDGE,"E22.filletArc");var subQ1=sQuery(id+"F0.wireOp",EDGE,"E7");var subQ2=sQuery(id+"F0.wireOp",EDGE,"E6");var subQ3=sQuery(id+"F0.wireOp",EDGE,"E5");var subQ4=sQuery(id+"F0.wireOp",EDGE,"E4");var subQ5=sQuery(id+"F0.wireOp",EDGE,"E1.bottom");var subQ6=sQuery(id+"F0.wireOp",EDGE,"E21.filletArc");var subQ7=sQuery(id+"F0.wireOp",EDGE,"E1.top");var subQ8=sQuery(id+"F0.wireOp",EDGE,"E1.left");var subQ9=sQuery(id+"F0.wireOp",EDGE,"E1.right");var subQ10=sQuery(id+"F0.wireOp",EDGE,"E23.filletArc");var subQ11=sQuery(id+"F0.wireOp",EDGE,"E24.filletArc");Q0=makeQuery(id+"F2.boolean.opBoolean","SPLIT",FACE,{"disambiguationData":[TD([makeQuery(id+"F1.opExtrude","SWEPT_FACE",FACE,{"disambiguationData":[OSD([subQ5])]})])],"derivedFrom":makeQuery(id+"F1.opExtrude","CAP_FACE",FACE,{"disambiguationData":[OSD([subQ5,subQ7,subQ8,subQ9,subQ4,subQ3,subQ2,subQ1,subQ6,subQ0,subQ10,subQ11])],"isStart":true})});}
            var sketch = newSketch(context, id + "F16", { "sketchPlane" : qUnion([Q0])});
            skArc(sketch, "E79.0", {"start": v(90, 70) * mm, "mid": v(87.07, 77.07) * mm, "end": v(80, 80) * mm});
            skLineSegment(sketch, "E79.1", {"start": v(-80, 80) * mm, "end": v(80, 80) * mm});
            skArc(sketch, "E79.2", {"start": v(-80, 80) * mm, "mid": v(-87.07, 77.07) * mm, "end": v(-90, 70) * mm});
            skLineSegment(sketch, "E79.3", {"start": v(-90, -70) * mm, "end": v(-90, 70) * mm});
            skArc(sketch, "E79.4", {"start": v(-90, -70) * mm, "mid": v(-87.07, -77.07) * mm, "end": v(-80, -80) * mm});
            skLineSegment(sketch, "E79.5", {"start": v(-80, -80) * mm, "end": v(80, -80) * mm});
            skArc(sketch, "E79.6", {"start": v(80, -80) * mm, "mid": v(87.07, -77.07) * mm, "end": v(90, -70) * mm});
            skLineSegment(sketch, "E79.7", {"start": v(90, -70) * mm, "end": v(90, 70) * mm});
            skCircle(sketch, "E79.8", {"center": v(60, -53.33) * mm, "radius": 4 * mm});
            skCircle(sketch, "E79.9", {"center": v(-60, -53.33) * mm, "radius": 4 * mm});
            skCircle(sketch, "E79.10", {"center": v(-60, 53.33) * mm, "radius": 4 * mm});
            skCircle(sketch, "E79.11", {"center": v(60, 53.33) * mm, "radius": 4 * mm});
            skArc(sketch, "E79.12", {"start": v(52.38, 47.01) * mm, "mid": v(0, 53.33) * mm, "end": v(-52.38, 47.01) * mm});
            skArc(sketch, "E79.13", {"start": v(60, 37.3) * mm, "mid": v(57.87, 43.47) * mm, "end": v(52.38, 47.01) * mm});
            skLineSegment(sketch, "E79.14", {"start": v(60, 37.3) * mm, "end": v(60, -37.3) * mm});
            skArc(sketch, "E79.15", {"start": v(52.38, -47.01) * mm, "mid": v(57.87, -43.47) * mm, "end": v(60, -37.3) * mm});
            skArc(sketch, "E79.16", {"start": v(-52.38, -47.01) * mm, "mid": v(0, -53.33) * mm, "end": v(52.38, -47.01) * mm});
            skArc(sketch, "E79.17", {"start": v(-60, -37.3) * mm, "mid": v(-57.87, -43.47) * mm, "end": v(-52.38, -47.01) * mm});
            skLineSegment(sketch, "E79.18", {"start": v(-60, 37.3) * mm, "end": v(-60, -37.3) * mm});
            skArc(sketch, "E79.19", {"start": v(-52.38, 47.01) * mm, "mid": v(-57.87, 43.47) * mm, "end": v(-60, 37.3) * mm});
            skArc(sketch, "E80", {"start": v(15, 110) * mm, "mid": v(0, 125) * mm, "end": v(-15, 110) * mm});
            skLineSegment(sketch, "E81", {"start": v(-15, 110) * mm, "end": v(-15, 98) * mm});
            skLineSegment(sketch, "E82", {"start": v(15, 110) * mm, "end": v(15, 98) * mm});
            skLineSegment(sketch, "E83", {"start": v(15, 98) * mm, "end": v(33, 80) * mm});
            skLineSegment(sketch, "E84", {"start": v(0, 80) * mm, "end": v(0, 110) * mm, "construction": true});
            skCircle(sketch, "E85", {"center": v(0, 110) * mm, "radius": 6 * mm});
            skLineSegment(sketch, "E86", {"start": v(-15, 98) * mm, "end": v(-33, 80) * mm});
            skLineSegment(sketch, "E87", {"start": v(-90, 0) * mm, "end": v(90, 0) * mm, "construction": true});
            skLineSegment(sketch, "E88.MirrorCS", {"start": v(15, -98) * mm, "end": v(33, -80) * mm});
            skLineSegment(sketch, "E89.MirrorCS", {"start": v(15, -110) * mm, "end": v(15, -98) * mm});
            skLineSegment(sketch, "E90.MirrorCS", {"start": v(0, -80) * mm, "end": v(0, -110) * mm, "construction": true});
            skArc(sketch, "E91.MirrorCS", {"start": v(15, -110) * mm, "mid": v(0, -125) * mm, "end": v(-15, -110) * mm});
            skLineSegment(sketch, "E92.MirrorCS", {"start": v(-15, -110) * mm, "end": v(-15, -98) * mm});
            skLineSegment(sketch, "E93.MirrorCS", {"start": v(-15, -98) * mm, "end": v(-33, -80) * mm});
            skCircle(sketch, "E94.MirrorC", {"center": v(0, -110) * mm, "radius": 6 * mm});
            skSolve(sketch);
        }
        {
            var Q0;
            Q0=makeQuery(id+"F16.imprint","IMPRINT",FACE,{"disambiguationData":[TD([[makeQuery(id+"F16.imprint","IMPRINT",EDGE,{"derivedFrom":sQuery(id+"F16.wireOp",EDGE,"E80")}),1.0]])]});
            var Q1;
            {var subQ2=sQuery(id+"F16.wireOp",EDGE,"E79.0");Q1=makeQuery(id+"F16.imprint","IMPRINT",FACE,{"disambiguationData":[TD([[makeQuery(id+"F16.imprint","IMPRINT",EDGE,{"derivedFrom":subQ2}),1.0]])]});}
            var Q2;
            Q2=makeQuery(id+"F16.imprint","IMPRINT",FACE,{"disambiguationData":[TD([[makeQuery(id+"F16.imprint","IMPRINT",EDGE,{"derivedFrom":sQuery(id+"F16.wireOp",EDGE,"E89.MirrorCS")}),1.0]])]});
            extrude(context, id + "F17", {"entities" : qUnion([Q0, Q1, Q2]), "operationType" : NewBodyOperationType.ADD, "endBound" : BoundingType.SYMMETRIC, "depth" : 6 * mm});
        }
    });
